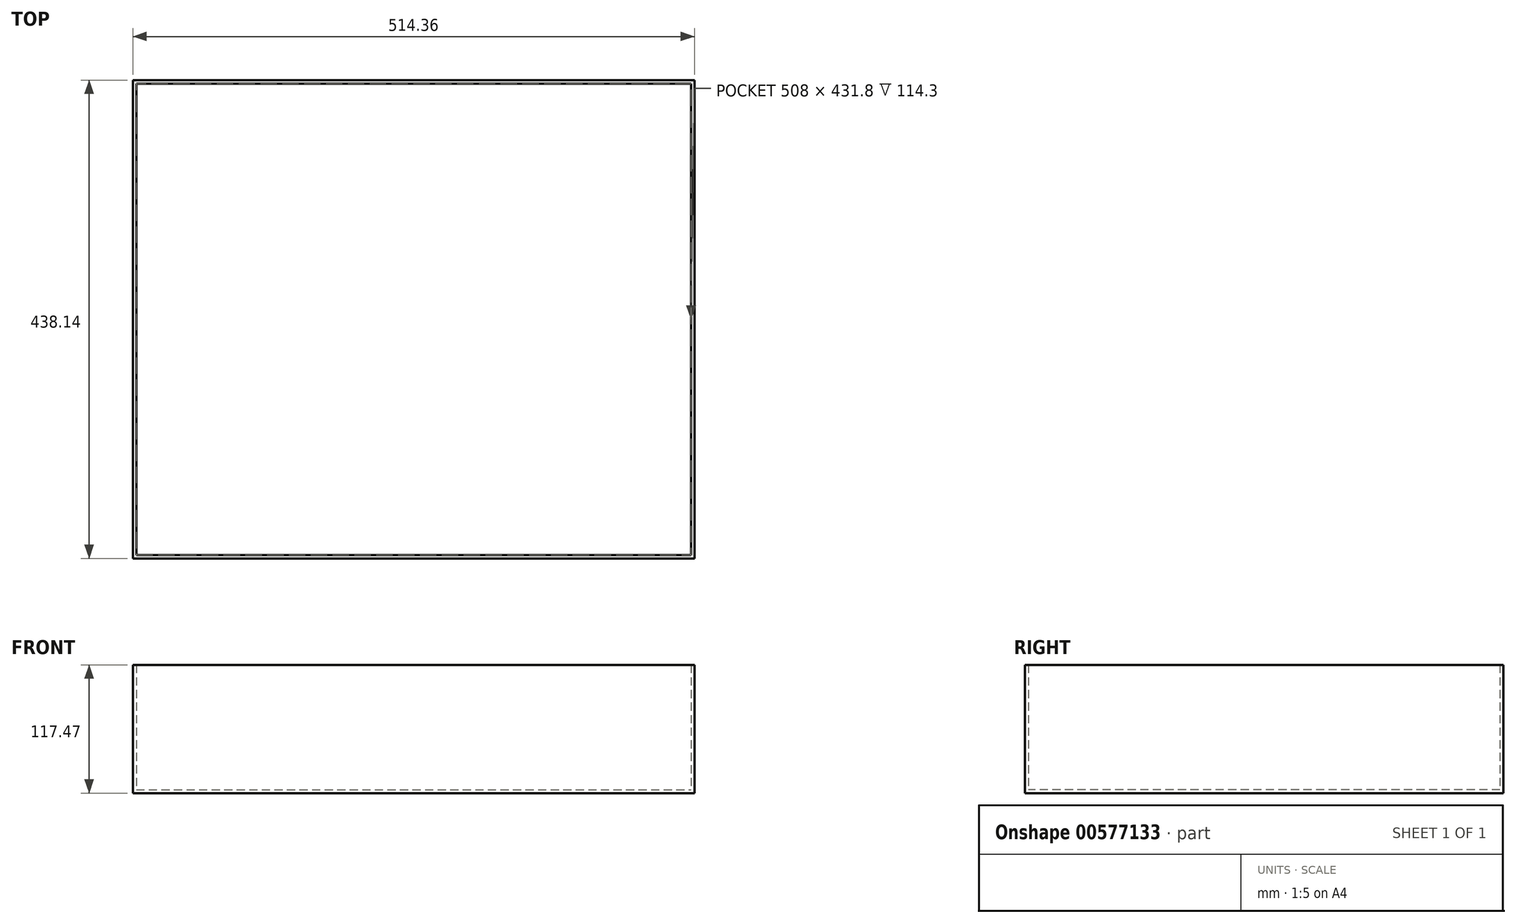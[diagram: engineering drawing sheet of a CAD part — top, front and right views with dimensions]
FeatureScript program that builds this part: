
annotation { "Feature Type Name" : "Feature", "Feature Type Description" : "" }
export const myFeature = defineFeature(function(context is Context, id is Id, definition is map)
    precondition{}
    {
        {
            var Q0;
            Q0=qCreatedBy(makeId("Top.planeOp"),FACE);
            var sketch = newSketch(context, id + "F0", { "sketchPlane" : qUnion([Q0])});
            skLineSegment(sketch, "E0.bottom", {"start": v(-254, 215.9) * mm, "end": v(254, 215.9) * mm});
            skLineSegment(sketch, "E0.top", {"start": v(-254, -215.9) * mm, "end": v(254, -215.9) * mm});
            skLineSegment(sketch, "E0.left", {"start": v(-254, 215.9) * mm, "end": v(-254, -215.9) * mm});
            skLineSegment(sketch, "E0.right", {"start": v(254, 215.9) * mm, "end": v(254, -215.9) * mm});
            skPoint(sketch, "E0.middle", {"position": v(0, 0) * mm});
            skSolve(sketch);
        }
        {
            var Q0;
            Q0 = qSketchRegion(id + "F0", true);
            extrude(context, id + "F1", {"entities" : qUnion([Q0]), "depth" : 114.3 * mm, "offsetDistance" : 25.4 * mm});
        }
        {
            var Q0;
            Q0=makeQuery(id+"F1.opExtrude","CAP_FACE",FACE,{"disambiguationData":[OSD([sQuery(id+"F0.wireOp",EDGE,"E0.bottom"),sQuery(id+"F0.wireOp",EDGE,"E0.top"),sQuery(id+"F0.wireOp",EDGE,"E0.left"),sQuery(id+"F0.wireOp",EDGE,"E0.right")])],"isStart":false});
            shell(context, id + "F2", {"entities" : qUnion([Q0]), "thickness" : 3.17 * mm, "oppositeDirection" : true});
        }
    });
